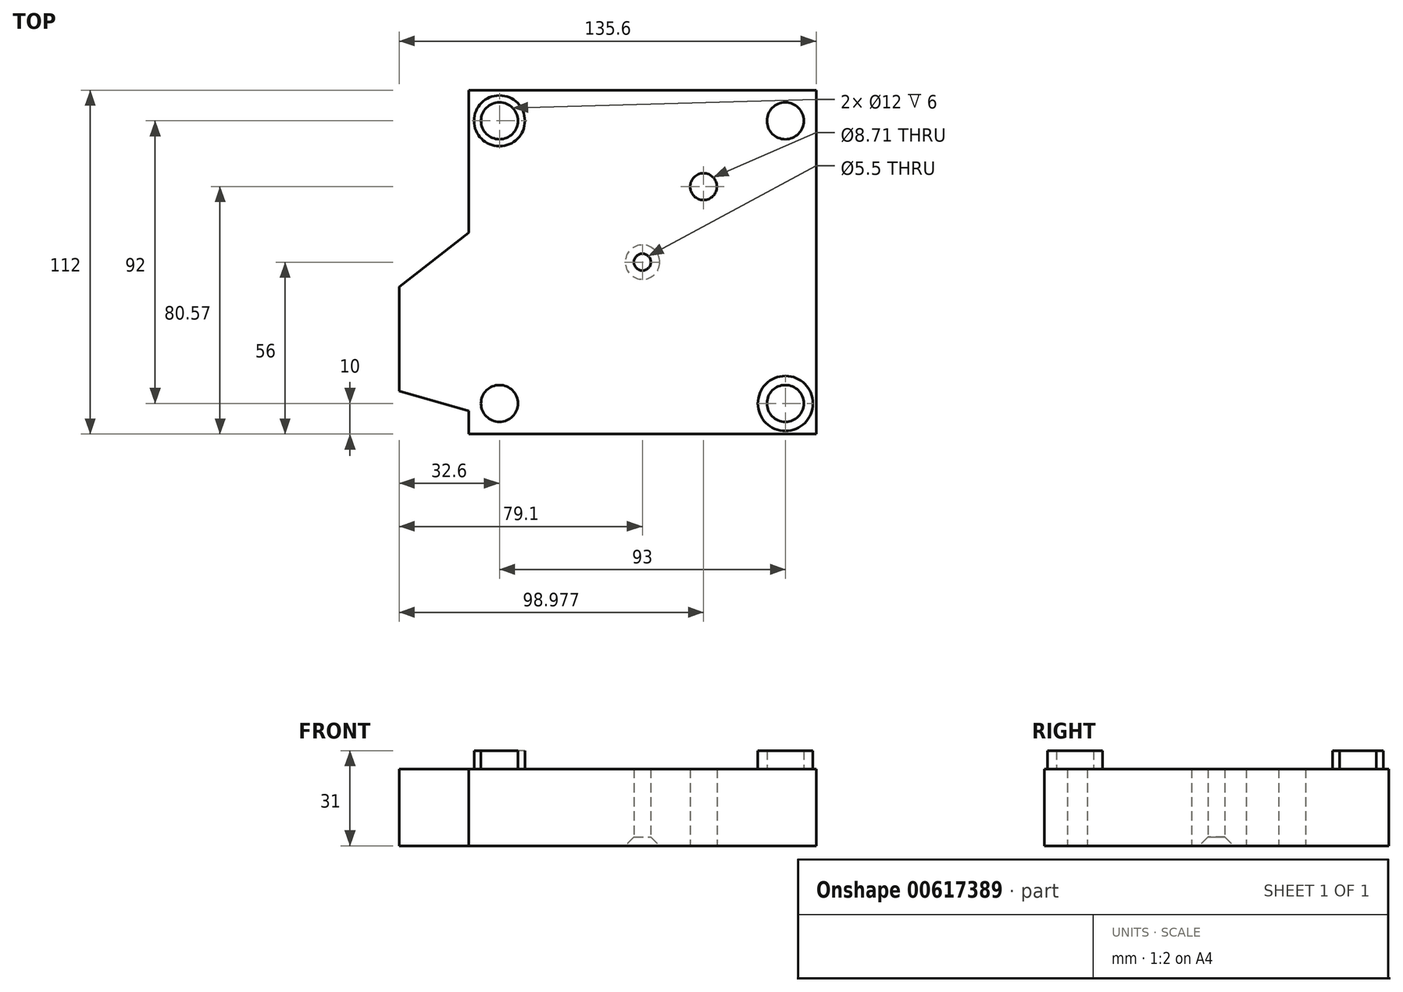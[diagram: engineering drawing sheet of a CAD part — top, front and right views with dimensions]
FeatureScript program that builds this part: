
annotation { "Feature Type Name" : "Feature", "Feature Type Description" : "" }
export const myFeature = defineFeature(function(context is Context, id is Id, definition is map)
    precondition{}
    {
        {
            var Q0;
            Q0=qCreatedBy(makeId("Top.planeOp"),FACE);
            var sketch = newSketch(context, id + "F0", { "sketchPlane" : qUnion([Q0])});
            skLineSegment(sketch, "E0.bottom", {"start": v(56.5, -56) * mm, "end": v(-56.5, -56) * mm});
            skLineSegment(sketch, "E0.top", {"start": v(56.5, 56) * mm, "end": v(-56.5, 56) * mm});
            skLineSegment(sketch, "E0.left", {"start": v(56.5, -56) * mm, "end": v(56.5, 56) * mm});
            skLineSegment(sketch, "E0.right", {"start": v(-56.5, -56) * mm, "end": v(-56.5, 56) * mm});
            skPoint(sketch, "E0.middle", {"position": v(0, 0) * mm});
            skLineSegment(sketch, "E1", {"start": v(-56.5, 9.65) * mm, "end": v(-79.1, -8.1) * mm});
            skLineSegment(sketch, "E2", {"start": v(-79.1, -8.1) * mm, "end": v(-79.1, -42) * mm});
            skLineSegment(sketch, "E3", {"start": v(-79.1, -42) * mm, "end": v(-56.5, -48.47) * mm});
            skCircle(sketch, "E4", {"center": v(-46.5, 46) * mm, "radius": 6 * mm});
            skCircle(sketch, "E5.MirrorC", {"center": v(46.5, 46) * mm, "radius": 6 * mm});
            skCircle(sketch, "E6.MirrorC", {"center": v(-46.5, -46) * mm, "radius": 6 * mm});
            skCircle(sketch, "E7.MirrorC", {"center": v(46.5, -46) * mm, "radius": 6 * mm});
            skCircle(sketch, "E8", {"center": v(-46.5, 46) * mm, "radius": 8.26 * mm});
            skCircle(sketch, "E9", {"center": v(46.5, 46) * mm, "radius": 8.49 * mm});
            skCircle(sketch, "E10", {"center": v(46.5, -46) * mm, "radius": 8.95 * mm});
            skCircle(sketch, "E11", {"center": v(-46.5, -46) * mm, "radius": 8.12 * mm});
            skSolve(sketch);
        }
        {
            var Q0;
            {var subQ1=sQuery(id+"F0.wireOp",EDGE,"E0.bottom");Q0=makeQuery(id+"F0.imprint","IMPRINT",FACE,{"disambiguationData":[TD([[makeQuery(id+"F0.imprint","IMPRINT",EDGE,{"derivedFrom":subQ1}),-1.0]])]});}
            var Q1;
            {var subQ0=sQuery(id+"F0.wireOp",EDGE,"E1");Q1=makeQuery(id+"F0.imprint","IMPRINT",FACE,{"disambiguationData":[TD([[makeQuery(id+"F0.imprint","IMPRINT",EDGE,{"derivedFrom":subQ0}),1.0]])]});}
            var Q2;
            Q2=makeQuery(id+"F0.imprint","IMPRINT",FACE,{"disambiguationData":[TD([[makeQuery(id+"F0.imprint","IMPRINT",EDGE,{"derivedFrom":sQuery(id+"F0.wireOp",EDGE,"E4")}),1.0]])]});
            var Q3;
            Q3=makeQuery(id+"F0.imprint","IMPRINT",FACE,{"disambiguationData":[TD([[makeQuery(id+"F0.imprint","IMPRINT",EDGE,{"derivedFrom":sQuery(id+"F0.wireOp",EDGE,"E5.MirrorC")}),-1.0]])]});
            var Q4;
            Q4=makeQuery(id+"F0.imprint","IMPRINT",FACE,{"disambiguationData":[TD([[makeQuery(id+"F0.imprint","IMPRINT",EDGE,{"derivedFrom":sQuery(id+"F0.wireOp",EDGE,"E7.MirrorC")}),1.0]])]});
            var Q5;
            Q5=makeQuery(id+"F0.imprint","IMPRINT",FACE,{"disambiguationData":[TD([[makeQuery(id+"F0.imprint","IMPRINT",EDGE,{"derivedFrom":sQuery(id+"F0.wireOp",EDGE,"E6.MirrorC")}),-1.0]])]});
            extrude(context, id + "F1", {"entities" : qUnion([Q0, Q1, Q2, Q3, Q4, Q5]), "depth" : 25 * mm, "offsetDistance" : 25 * mm});
        }
        {
            var Q0;
            Q0=makeQuery(id+"F0.imprint","IMPRINT",FACE,{"disambiguationData":[TD([[makeQuery(id+"F0.imprint","IMPRINT",EDGE,{"derivedFrom":sQuery(id+"F0.wireOp",EDGE,"E6.MirrorC")}),1.0]])]});
            var Q1;
            Q1=makeQuery(id+"F0.imprint","IMPRINT",FACE,{"disambiguationData":[TD([[makeQuery(id+"F0.imprint","IMPRINT",EDGE,{"derivedFrom":sQuery(id+"F0.wireOp",EDGE,"E7.MirrorC")}),-1.0]])]});
            var Q2;
            Q2=makeQuery(id+"F0.imprint","IMPRINT",FACE,{"disambiguationData":[TD([[makeQuery(id+"F0.imprint","IMPRINT",EDGE,{"derivedFrom":sQuery(id+"F0.wireOp",EDGE,"E5.MirrorC")}),1.0]])]});
            var Q3;
            Q3=makeQuery(id+"F0.imprint","IMPRINT",FACE,{"disambiguationData":[TD([[makeQuery(id+"F0.imprint","IMPRINT",EDGE,{"derivedFrom":sQuery(id+"F0.wireOp",EDGE,"E4")}),-1.0]])]});
            extrude(context, id + "F2", {"entities" : qUnion([Q0, Q1, Q2, Q3]), "operationType" : NewBodyOperationType.ADD, "depth" : 31 * mm, "offsetDistance" : 25 * mm});
        }
        {
            var Q0;
            Q0=qCreatedBy(makeId("Top.planeOp"),FACE);
            var sketch = newSketch(context, id + "F3", { "sketchPlane" : qUnion([Q0])});
            skCircle(sketch, "E12", {"center": v(19.88, 24.57) * mm, "radius": 4.36 * mm});
            skSolve(sketch);
        }
        {
            var Q0;
            Q0=makeQuery(id+"F3.imprint","IMPRINT",FACE,{"disambiguationData":[TD([[makeQuery(id+"F3.imprint","IMPRINT",EDGE,{"derivedFrom":sQuery(id+"F3.wireOp",EDGE,"E12")}),1.0]])]});
            var Q1;
            Q1=sQuery(id+"F3.wireOp",EDGE,"E12");
            extrude(context, id + "F4", {"entities" : qUnion([Q0]), "operationType" : NewBodyOperationType.REMOVE, "surfaceEntities" : qUnion([Q1]), "endBound" : BoundingType.UP_TO_NEXT, "depth" : 25 * mm, "offsetDistance" : 25 * mm});
        }
        {
            var Q0;
            Q0=sQuery(id+"F0.wireOp",VERTEX,"E0.middle");
            var Q1;
            Q1=makeQuery(id+"F1.opExtrude","SWEPT_BODY",BODY,{"disambiguationData":[OSD([sQuery(id+"F0.wireOp",EDGE,"E0.bottom"),sQuery(id+"F0.wireOp",EDGE,"E0.top"),sQuery(id+"F0.wireOp",EDGE,"E0.left"),sQuery(id+"F0.wireOp",EDGE,"E0.right"),sQuery(id+"F0.wireOp",EDGE,"E1"),sQuery(id+"F0.wireOp",EDGE,"E2"),sQuery(id+"F0.wireOp",EDGE,"E3"),sQuery(id+"F0.wireOp",EDGE,"E8"),sQuery(id+"F0.wireOp",EDGE,"E9"),sQuery(id+"F0.wireOp",EDGE,"E10"),sQuery(id+"F0.wireOp",EDGE,"E11")])]});
            hole(context, id + "F5", {"style" : HoleStyle.C_SINK, "endStyle" : HoleEndStyle.THROUGH, "oppositeDirection" : true, "standardTappedOrClearance" : lookupTablePath({ "standard" : "ISO", "fit" : "Normal", "size" : "M5", "type" : "Clearance" }), "standardBlindInLast" : lookupTablePath({ "fit" : "Standard", "standard" : "ISO", "size" : "M5", "type" : "Clearance" }), "holeDiameter" : 5.5 * mm, "cSinkDiameter" : 11.2 * mm, "cSinkAngle" : 90 * degree, "majorDiameter" : 5 * mm, "isTappedThrough" : true, "tappedDepth" : 12 * mm, "tapClearance" : 3, "locations" : qUnion([Q0]), "scope" : qUnion([Q1])});
        }
    });
